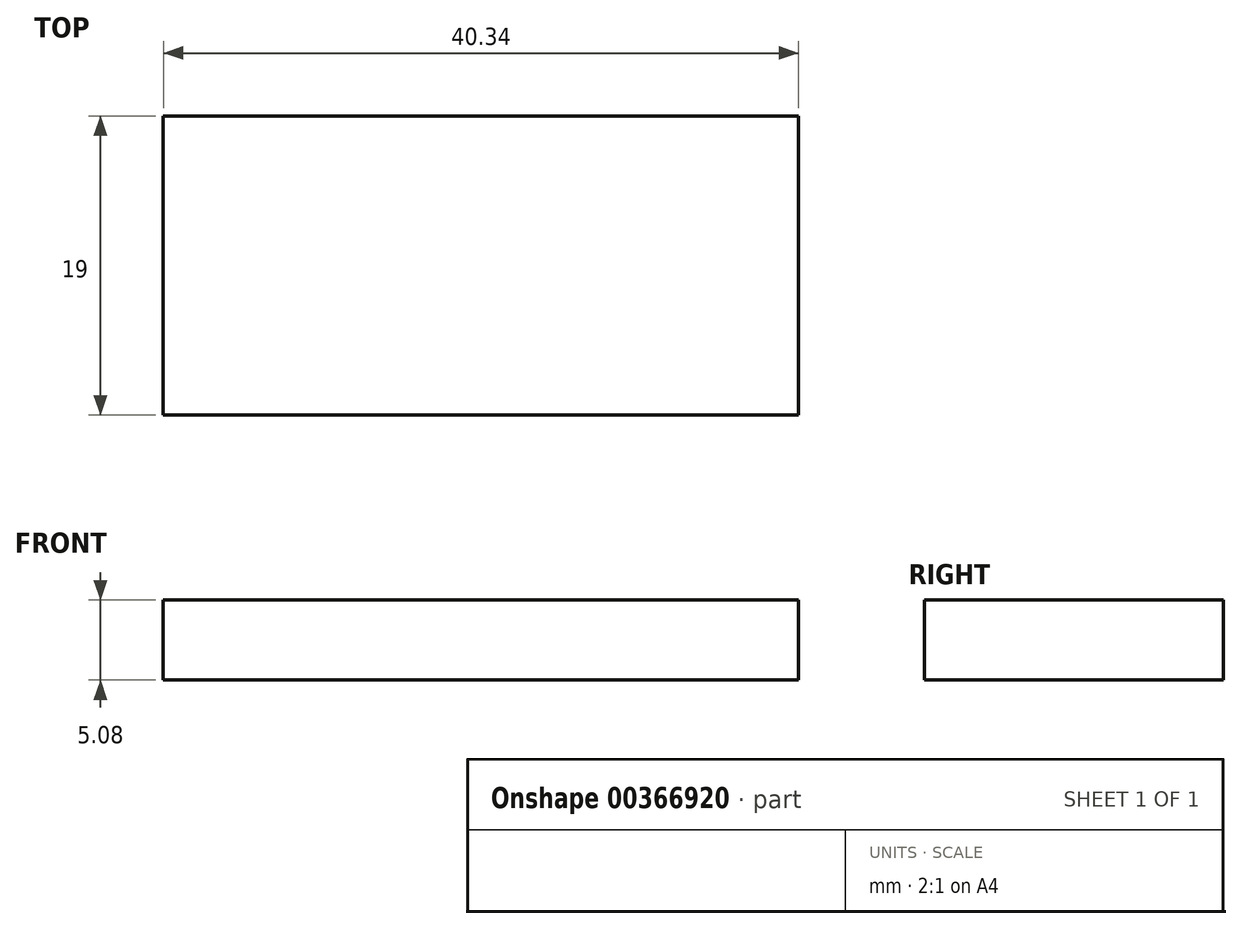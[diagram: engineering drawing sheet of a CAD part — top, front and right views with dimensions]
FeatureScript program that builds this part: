
annotation { "Feature Type Name" : "Feature", "Feature Type Description" : "" }
export const myFeature = defineFeature(function(context is Context, id is Id, definition is map)
    precondition{}
    {
        {
            var Q0;
            Q0=qCreatedBy(makeId("Top.planeOp"),FACE);
            var sketch = newSketch(context, id + "F0", { "sketchPlane" : qUnion([Q0])});
            skLineSegment(sketch, "E0.bottom", {"start": v(-20.17, -9.5) * mm, "end": v(20.17, -9.5) * mm});
            skLineSegment(sketch, "E0.top", {"start": v(-20.17, 9.5) * mm, "end": v(20.17, 9.5) * mm});
            skLineSegment(sketch, "E0.left", {"start": v(-20.17, -9.5) * mm, "end": v(-20.17, 9.5) * mm});
            skLineSegment(sketch, "E0.right", {"start": v(20.17, -9.5) * mm, "end": v(20.17, 9.5) * mm});
            skPoint(sketch, "E0.middle", {"position": v(0, 0) * mm});
            skSolve(sketch);
        }
        {
            var Q0;
            Q0=makeQuery(id+"F0.imprint","IMPRINT",FACE,{"disambiguationData":[TD([[makeQuery(id+"F0.imprint","IMPRINT",EDGE,{"derivedFrom":sQuery(id+"F0.wireOp",EDGE,"E0.bottom")}),1.0]])]});
            extrude(context, id + "F1", {"entities" : qUnion([Q0]), "depth" : 5.08 * mm});
        }
    });
